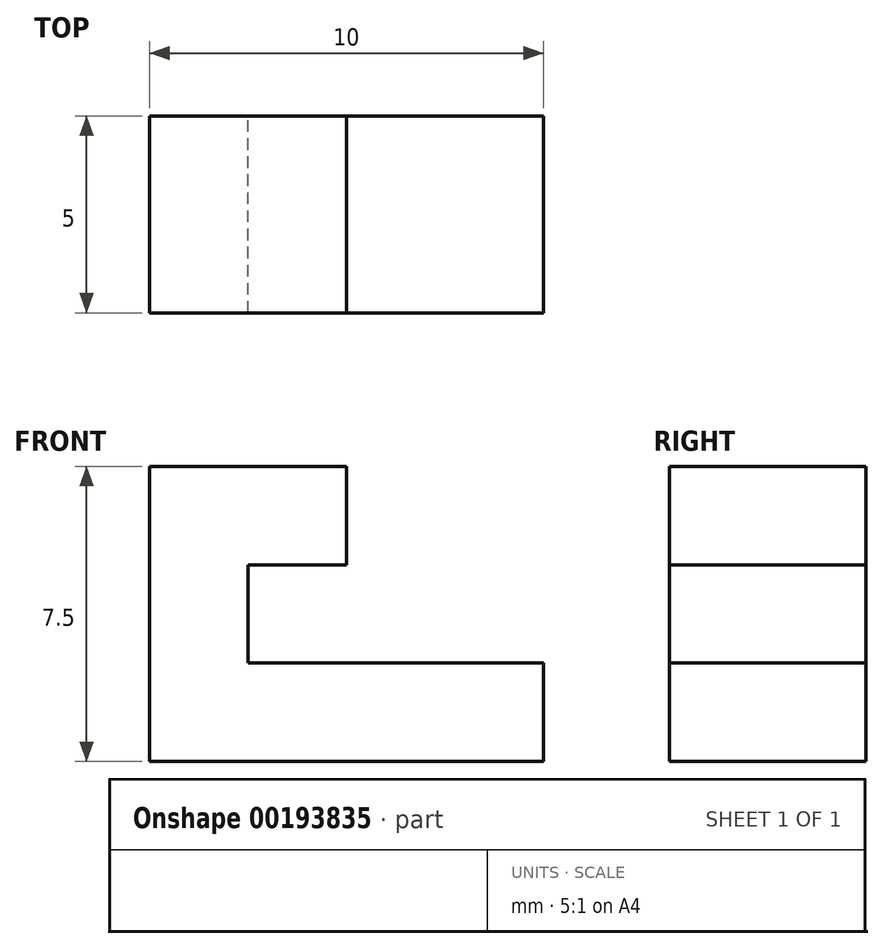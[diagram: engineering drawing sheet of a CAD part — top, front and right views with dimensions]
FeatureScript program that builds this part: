
annotation { "Feature Type Name" : "Feature", "Feature Type Description" : "" }
export const myFeature = defineFeature(function(context is Context, id is Id, definition is map)
    precondition{}
    {
        {
            var Q0;
            Q0=qCreatedBy(makeId("Front.planeOp"),FACE);
            var sketch = newSketch(context, id + "F0", { "sketchPlane" : qUnion([Q0])});
            skLineSegment(sketch, "E0", {"start": v(0, 0) * mm, "end": v(10, 0) * mm});
            skLineSegment(sketch, "E1", {"start": v(10, 0) * mm, "end": v(10, 2.5) * mm});
            skLineSegment(sketch, "E2", {"start": v(0, 0) * mm, "end": v(0, 7.5) * mm});
            skLineSegment(sketch, "E3", {"start": v(10, 2.5) * mm, "end": v(2.5, 2.5) * mm});
            skLineSegment(sketch, "E4", {"start": v(0, 7.5) * mm, "end": v(5, 7.5) * mm});
            skLineSegment(sketch, "E5", {"start": v(5, 7.5) * mm, "end": v(5, 5) * mm});
            skLineSegment(sketch, "E6", {"start": v(5, 5) * mm, "end": v(2.5, 5) * mm});
            skLineSegment(sketch, "E7", {"start": v(2.5, 5) * mm, "end": v(2.5, 2.5) * mm});
            skSolve(sketch);
        }
        {
            var Q0;
            Q0 = qSketchRegion(id + "F0", true);
            extrude(context, id + "F1", {"entities" : qUnion([Q0]), "endBound" : BoundingType.SYMMETRIC, "depth" : 5 * mm});
        }
    });
